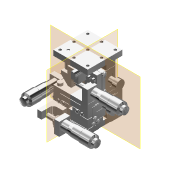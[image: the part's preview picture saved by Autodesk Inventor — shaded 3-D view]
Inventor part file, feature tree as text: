
AUTODESK INVENTOR PART (.ipt)
format: ipt  version: 2022 (Build 260153000, 153)  size: 822,272 bytes
history: native  units: mm
features: other x8, plane x2, extrude x1, sketch x1, projected_geometry x1
ambient origin geometry x8: Origin, YZ Plane, XZ Plane, XY Plane, X Axis, Y Axis, Z Axis, Center Point
bodies: Volumenkörper1 (feature_tree), Volumenkörper2 (feature_tree), Volumenkörper3 (feature_tree), Volumenkörper4 (feature_tree), Volumenkörper5 (feature_tree), Volumenkörper6 (feature_tree), Volumenkörper7 (feature_tree), Volumenkörper8 (feature_tree)
feature tree (13):
  other  "LT-4047-S1-4_1:1"
  other  "LT-4047-S1-6_3:1"
  plane  "Arbeitsebene1"
  plane  "Arbeitsebene2"
  extrude  "Extrusion1"  Depth=10.0mm
  sketch  "Skizze1"  dims[d0=2.8mm d1=2.8mm d2=10.0mm d3=20.0mm d4=10.0mm d5=0.0mm]
  projected_geometry  "Projizierte Kontur1"
  other  "LT-4047-S1-3_2:1"
  other  "LT-4047-S1-3_2:2"
  other  "LT-4047-S1-5_4:1"
  other  "LT-4047-S1-1_5:1"
  other  "LT-4047-S1-2_6:1"
  other  "LT-4047-S1-2_6:2"
